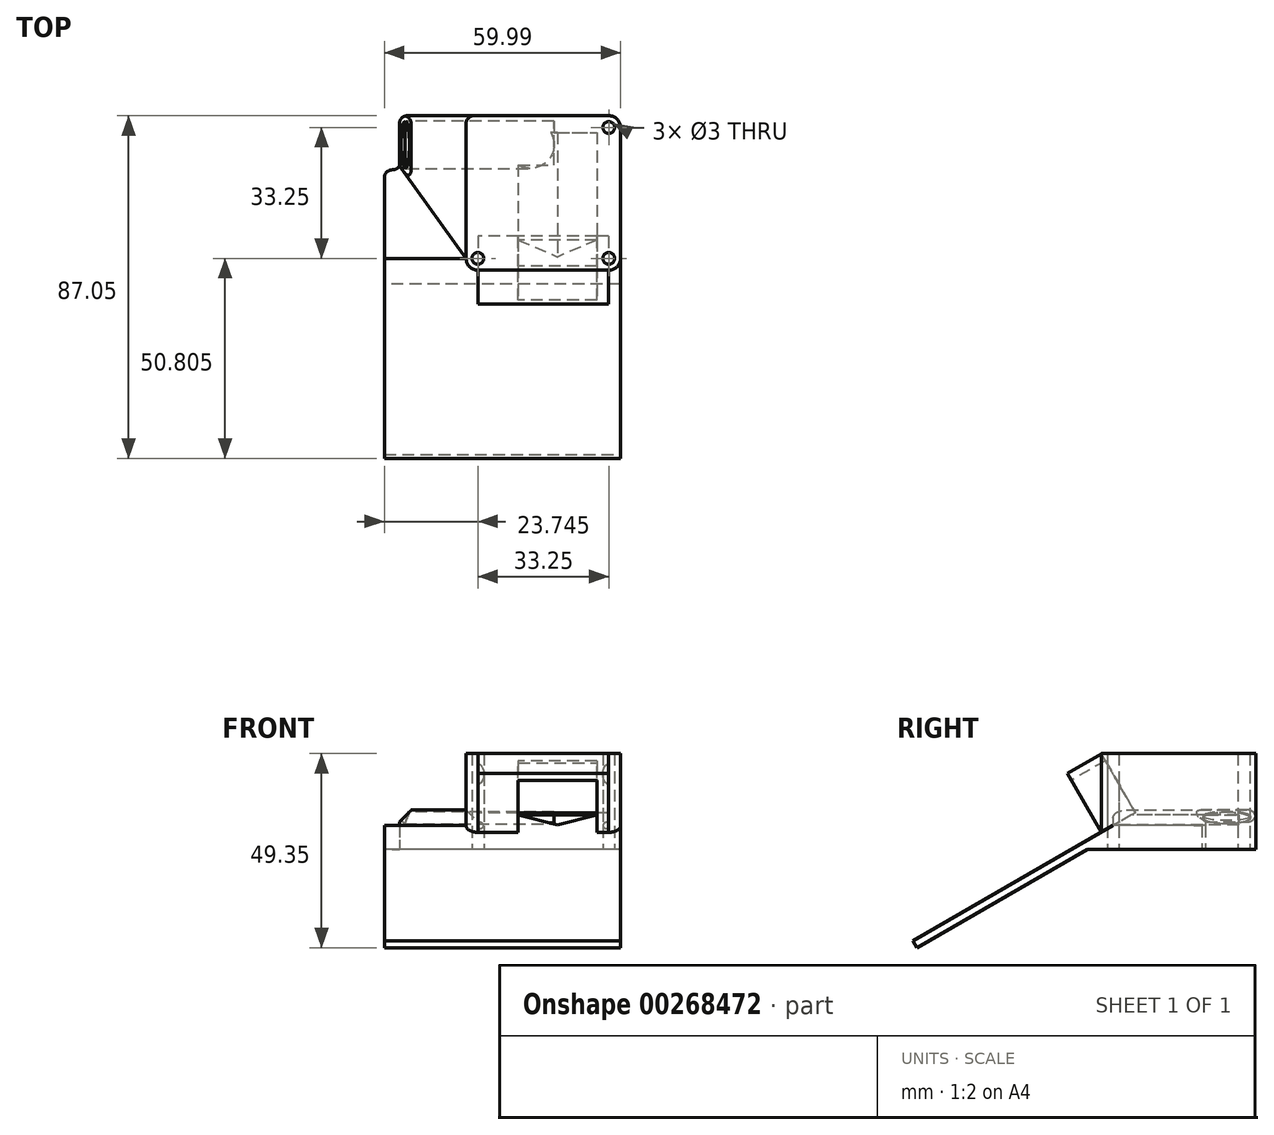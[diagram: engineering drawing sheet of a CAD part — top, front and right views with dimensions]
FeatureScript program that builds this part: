
annotation { "Feature Type Name" : "Feature", "Feature Type Description" : "" }
export const myFeature = defineFeature(function(context is Context, id is Id, definition is map)
    precondition{}
    {
        {
            var Q0;
            Q0=qCreatedBy(makeId("Top.planeOp"),FACE);
            var sketch = newSketch(context, id + "F0", { "sketchPlane" : qUnion([Q0])});
            skLineSegment(sketch, "E0.bottom", {"start": v(34.17, 23.12) * mm, "end": v(-34.17, 23.12) * mm});
            skLineSegment(sketch, "E0.top", {"start": v(34.17, -23.12) * mm, "end": v(-34.17, -23.12) * mm});
            skLineSegment(sketch, "E0.left", {"start": v(34.17, 23.12) * mm, "end": v(34.17, -23.12) * mm});
            skLineSegment(sketch, "E0.right", {"start": v(-34.17, 23.12) * mm, "end": v(-34.17, -23.12) * mm});
            skPoint(sketch, "E0.middle", {"position": v(0, 0) * mm});
            skCircle(sketch, "E1", {"center": v(31.18, -16.62) * mm, "radius": 1.28 * mm});
            skLineSegment(sketch, "E2", {"start": v(-54.01, 0) * mm, "end": v(41.89, 0) * mm, "construction": true});
            skPoint(sketch, "E2.endSnap0", {"position": v(34.17, 0) * mm});
            skCircle(sketch, "E3.MirrorC", {"center": v(31.17, 16.63) * mm, "radius": 1.28 * mm});
            skCircle(sketch, "E4", {"center": v(-2.08, -16.62) * mm, "radius": 1.25 * mm});
            skCircle(sketch, "E5", {"center": v(-28.3, 15.75) * mm, "radius": 3.88 * mm});
            skCircle(sketch, "E6", {"center": v(-31.17, -14.12) * mm, "radius": 1.5 * mm});
            skCircle(sketch, "E7.0.1.0", {"center": v(-31.17, 5.88) * mm, "radius": 1.5 * mm});
            skCircle(sketch, "E7.1.0.0", {"center": v(-13.17, -14.12) * mm, "radius": 1.5 * mm});
            skCircle(sketch, "E7.1.1.0", {"center": v(-13.17, 5.88) * mm, "radius": 1.5 * mm});
            skLineSegment(sketch, "E7.direction1", {"start": v(-31.17, -14.12) * mm, "end": v(-13.17, -14.12) * mm, "construction": true});
            skLineSegment(sketch, "E7.direction2", {"start": v(-31.17, -14.12) * mm, "end": v(-31.17, 5.88) * mm, "construction": true});
            skCircle(sketch, "E8", {"center": v(15.67, 0) * mm, "radius": 7.5 * mm});
            skSolve(sketch);
        }
        {
            var Q0;
            Q0 = qSketchRegion(id + "F0", true);
            extrude(context, id + "F1", {"entities" : qUnion([Q0]), "depth" : 8 * mm, "offsetDistance" : 25 * mm});
        }
        {
            var Q0;
            Q0=makeQuery(id+"F1.opExtrude","CAP_FACE",FACE,{"disambiguationData":[OSD([sQuery(id+"F0.wireOp",EDGE,"E0.bottom"),sQuery(id+"F0.wireOp",EDGE,"E0.top"),sQuery(id+"F0.wireOp",EDGE,"E0.left"),sQuery(id+"F0.wireOp",EDGE,"E0.right"),sQuery(id+"F0.wireOp",EDGE,"E1"),sQuery(id+"F0.wireOp",EDGE,"E3.MirrorC"),sQuery(id+"F0.wireOp",EDGE,"E4"),sQuery(id+"F0.wireOp",EDGE,"E5"),sQuery(id+"F0.wireOp",EDGE,"E6"),sQuery(id+"F0.wireOp",EDGE,"E7.0.1.0"),sQuery(id+"F0.wireOp",EDGE,"E7.1.0.0"),sQuery(id+"F0.wireOp",EDGE,"E7.1.1.0"),sQuery(id+"F0.wireOp",EDGE,"E8")])],"isStart":false});
            var sketch = newSketch(context, id + "F2", { "sketchPlane" : qUnion([Q0])});
            skCircle(sketch, "E9", {"center": v(-2.08, -16.62) * mm, "radius": 3 * mm});
            skCircle(sketch, "E10", {"center": v(31.18, -16.62) * mm, "radius": 3 * mm});
            skCircle(sketch, "E11", {"center": v(31.17, 16.63) * mm, "radius": 3 * mm});
            skCircle(sketch, "E12", {"center": v(-2.08, -16.62) * mm, "radius": 1.5 * mm});
            skCircle(sketch, "E13", {"center": v(31.18, -16.62) * mm, "radius": 1.5 * mm});
            skCircle(sketch, "E14", {"center": v(31.17, 16.63) * mm, "radius": 1.5 * mm});
            skLineSegment(sketch, "E15.bottom", {"start": v(-2.08, -19.62) * mm, "end": v(31.17, -19.62) * mm});
            skLineSegment(sketch, "E16.left", {"start": v(-5.08, -16.62) * mm, "end": v(-5.08, 19.63) * mm});
            skLineSegment(sketch, "E17", {"start": v(34.17, -16.62) * mm, "end": v(34.17, 16.63) * mm});
            skLineSegment(sketch, "E18", {"start": v(31.17, 19.63) * mm, "end": v(-5.08, 19.63) * mm});
            skLineSegment(sketch, "E19.bottom", {"start": v(28.17, 16.63) * mm, "end": v(0.92, 16.63) * mm});
            skLineSegment(sketch, "E19.top", {"start": v(28.17, -16.62) * mm, "end": v(0.92, -16.62) * mm});
            skLineSegment(sketch, "E19.left", {"start": v(28.17, 16.63) * mm, "end": v(28.17, -16.62) * mm});
            skLineSegment(sketch, "E19.right", {"start": v(0.92, 16.63) * mm, "end": v(0.92, -16.62) * mm});
            skLineSegment(sketch, "E20", {"start": v(-5.08, -16.62) * mm, "end": v(-22, 6.86) * mm});
            skLineSegment(sketch, "E21", {"start": v(-22, 6.86) * mm, "end": v(-22, 19.63) * mm});
            skLineSegment(sketch, "E22", {"start": v(-22, 19.63) * mm, "end": v(-5.08, 19.63) * mm});
            skSolve(sketch);
        }
        {
            var Q0;
            Q0=makeQuery(id+"F2.imprint","IMPRINT",FACE,{"disambiguationData":[TD([[makeQuery(id+"F2.imprint","IMPRINT",EDGE,{"derivedFrom":sQuery(id+"F2.wireOp",EDGE,"E14")}),-1.0]])]});
            var Q1;
            Q1=makeQuery(id+"F2.imprint","IMPRINT",FACE,{"disambiguationData":[TD([[makeQuery(id+"F2.imprint","IMPRINT",EDGE,{"derivedFrom":sQuery(id+"F2.wireOp",EDGE,"E13")}),-1.0]])]});
            var Q2;
            {var subQ0=sQuery(id+"F2.wireOp",EDGE,"E17");Q2=makeQuery(id+"F2.imprint","IMPRINT",FACE,{"disambiguationData":[TD([[makeQuery(id+"F2.imprint","IMPRINT",EDGE,{"derivedFrom":subQ0}),-1.0]])]});}
            var Q3;
            {var subQ0=sQuery(id+"F2.wireOp",EDGE,"E16.left");Q3=makeQuery(id+"F2.imprint","IMPRINT",FACE,{"disambiguationData":[TD([[makeQuery(id+"F2.imprint","IMPRINT",EDGE,{"derivedFrom":subQ0}),-1.0]])]});}
            var Q4;
            Q4=makeQuery(id+"F2.imprint","IMPRINT",FACE,{"disambiguationData":[TD([[makeQuery(id+"F2.imprint","IMPRINT",EDGE,{"derivedFrom":sQuery(id+"F2.wireOp",EDGE,"E19.bottom")}),1.0]])]});
            var Q5;
            Q5=makeQuery(id+"F2.imprint","IMPRINT",FACE,{"disambiguationData":[TD([[makeQuery(id+"F2.imprint","IMPRINT",EDGE,{"derivedFrom":makeQuery(id+"F1.opExtrude","CAP_EDGE",EDGE,{"disambiguationData":[OSD([sQuery(id+"F0.wireOp",EDGE,"E8")])],"isStart":false})}),1.0]])]});
            var Q6;
            {var subQ0=sQuery(id+"F2.wireOp",EDGE,"E15.bottom");Q6=makeQuery(id+"F2.imprint","IMPRINT",FACE,{"disambiguationData":[TD([[makeQuery(id+"F2.imprint","IMPRINT",EDGE,{"derivedFrom":subQ0}),1.0]])]});}
            var Q7;
            Q7=makeQuery(id+"F2.imprint","IMPRINT",FACE,{"disambiguationData":[TD([[makeQuery(id+"F2.imprint","IMPRINT",EDGE,{"derivedFrom":sQuery(id+"F2.wireOp",EDGE,"E12")}),-1.0]])]});
            extrude(context, id + "F3", {"entities" : qUnion([Q0, Q1, Q2, Q3, Q4, Q5, Q6, Q7]), "operationType" : NewBodyOperationType.ADD, "depth" : 24.35 * mm, "offsetDistance" : 25 * mm});
        }
        {
            var Q0;
            Q0=makeQuery(id+"F3.boolean.opBoolean","MERGE",FACE,{"derivedFrom":[makeQuery(id+"F1.opExtrude","SWEPT_FACE",FACE,{"disambiguationData":[OSD([sQuery(id+"F0.wireOp",EDGE,"E0.left")])]}),makeQuery(id+"F3.opExtrude","SWEPT_FACE",FACE,{"disambiguationData":[OSD([sQuery(id+"F2.wireOp",EDGE,"E17")])]})]});
            var sketch = newSketch(context, id + "F4", { "sketchPlane" : qUnion([Q0])});
            skLineSegment(sketch, "E23", {"start": v(-23.12, 8) * mm, "end": v(-66.43, -17) * mm});
            skLineSegment(sketch, "E24", {"start": v(-23.12, 8) * mm, "end": v(-16.62, 11.75) * mm});
            skLineSegment(sketch, "E25", {"start": v(-66.43, -17) * mm, "end": v(-67.43, -15.27) * mm});
            skLineSegment(sketch, "E26", {"start": v(-67.43, -15.27) * mm, "end": v(-16.62, 14.06) * mm});
            skLineSegment(sketch, "E27", {"start": v(-16.62, 14.06) * mm, "end": v(-16.62, 11.75) * mm});
            skLineSegment(sketch, "E28", {"start": v(-16.62, 11.75) * mm, "end": v(-16.62, 8) * mm});
            skLineSegment(sketch, "E29", {"start": v(-16.62, 8) * mm, "end": v(-23.12, 8) * mm});
            skSolve(sketch);
        }
        {
            var Q0;
            Q0 = qSketchRegion(id + "F4", true);
            extrude(context, id + "F5", {"entities" : qUnion([Q0]), "operationType" : NewBodyOperationType.ADD, "oppositeDirection" : true, "depth" : 60 * mm, "offsetDistance" : 25 * mm});
        }
        {
            var Q0;
            {var subQ3=sQuery(id+"F4.wireOp",EDGE,"E26");Q0=makeQuery(id+"F5.boolean.opBoolean","SPLIT",FACE,{"disambiguationData":[TD([makeQuery(id+"F1.opExtrude","SWEPT_FACE",FACE,{"disambiguationData":[OSD([sQuery(id+"F0.wireOp",EDGE,"E0.left")])]})])],"derivedFrom":makeQuery(id+"F5.opExtrude","SWEPT_FACE",FACE,{"disambiguationData":[OSD([subQ3])]})});}
            var sketch = newSketch(context, id + "F6", { "sketchPlane" : qUnion([Q0])});
            skLineSegment(sketch, "E30.bottom", {"start": v(28.17, -10.83) * mm, "end": v(8.17, -10.83) * mm});
            skLineSegment(sketch, "E30.top", {"start": v(28.17, -16.91) * mm, "end": v(8.18, -16.91) * mm});
            skLineSegment(sketch, "E30.left", {"start": v(28.17, -10.83) * mm, "end": v(28.17, -16.91) * mm});
            skLineSegment(sketch, "E30.right", {"start": v(8.17, -10.83) * mm, "end": v(8.18, -16.91) * mm});
            skSolve(sketch);
        }
        {
            var Q0;
            Q0=makeQuery(id+"F6.imprint","IMPRINT",FACE,{"disambiguationData":[TD([[makeQuery(id+"F6.imprint","IMPRINT",EDGE,{"derivedFrom":sQuery(id+"F6.wireOp",EDGE,"E30.bottom")}),1.0]])]});
            extrude(context, id + "F7", {"entities" : qUnion([Q0]), "operationType" : NewBodyOperationType.ADD, "depth" : 15.25 * mm, "offsetDistance" : 25 * mm});
        }
        {
            var Q0;
            Q0=makeQuery(id+"F7.opExtrude","SWEPT_FACE",FACE,{"disambiguationData":[OSD([sQuery(id+"F6.wireOp",EDGE,"E30.bottom")])]});
            var sketch = newSketch(context, id + "F8", { "sketchPlane" : qUnion([Q0])});
            skLineSegment(sketch, "E31.bottom", {"start": v(-28.17, 20.5) * mm, "end": v(-8.17, 20.5) * mm});
            skLineSegment(sketch, "E31.top", {"start": v(-28.18, 35.74) * mm, "end": v(-8.17, 35.74) * mm});
            skLineSegment(sketch, "E31.left", {"start": v(-28.18, 20.5) * mm, "end": v(-28.18, 35.74) * mm});
            skLineSegment(sketch, "E31.right", {"start": v(-8.17, 20.5) * mm, "end": v(-8.17, 35.74) * mm});
            skLineSegment(sketch, "E32.bottom", {"start": v(-31.17, 20.5) * mm, "end": v(2.05, 20.5) * mm});
            skLineSegment(sketch, "E32.top", {"start": v(-31.17, 35.74) * mm, "end": v(2.05, 35.74) * mm});
            skLineSegment(sketch, "E32.left", {"start": v(-31.17, 20.5) * mm, "end": v(-31.17, 35.74) * mm});
            skLineSegment(sketch, "E32.right", {"start": v(2.05, 20.5) * mm, "end": v(2.05, 35.74) * mm});
            skLineSegment(sketch, "E33.bottom", {"start": v(2.05, 35.74) * mm, "end": v(-31.17, 35.74) * mm});
            skLineSegment(sketch, "E33.top", {"start": v(2.05, 37.74) * mm, "end": v(-31.17, 37.74) * mm});
            skLineSegment(sketch, "E33.left", {"start": v(2.05, 35.74) * mm, "end": v(2.05, 37.74) * mm});
            skLineSegment(sketch, "E33.right", {"start": v(-31.17, 35.74) * mm, "end": v(-31.17, 37.74) * mm});
            skSolve(sketch);
        }
        {
            var Q0;
            Q0 = qSketchRegion(id + "F6", true);
            extrude(context, id + "F9", {"entities" : qUnion([Q0]), "operationType" : NewBodyOperationType.REMOVE, "depth" : 25 * mm, "offsetDistance" : 25 * mm});
        }
        {
            var Q0;
            {var subQ0=sQuery(id+"F8.wireOp",EDGE,"E31.right");Q0=makeQuery(id+"F8.imprint","IMPRINT",FACE,{"disambiguationData":[TD([[makeQuery(id+"F8.imprint","IMPRINT",EDGE,{"derivedFrom":subQ0}),1.0]])]});}
            var Q1;
            {var subQ0=sQuery(id+"F8.wireOp",EDGE,"E31.left");Q1=makeQuery(id+"F8.imprint","IMPRINT",FACE,{"disambiguationData":[TD([[makeQuery(id+"F8.imprint","IMPRINT",EDGE,{"derivedFrom":subQ0}),-1.0]])]});}
            var Q2;
            Q2=makeQuery(id+"F8.imprint","IMPRINT",FACE,{"disambiguationData":[TD([[makeQuery(id+"F8.imprint","IMPRINT",EDGE,{"derivedFrom":sQuery(id+"F8.wireOp",EDGE,"E33.top")}),1.0]])]});
            extrude(context, id + "F10", {"entities" : qUnion([Q0, Q1, Q2]), "depth" : 10 * mm, "offsetDistance" : 25 * mm});
        }
        {
            var Q0;
            {var subQ0=sQuery(id+"F8.wireOp",EDGE,"E31.left");Q0=makeQuery(id+"F8.imprint","IMPRINT",FACE,{"disambiguationData":[TD([[makeQuery(id+"F8.imprint","IMPRINT",EDGE,{"derivedFrom":subQ0}),1.0]])]});}
            extrude(context, id + "F11", {"entities" : qUnion([Q0]), "operationType" : NewBodyOperationType.REMOVE, "depth" : 10 * mm, "offsetDistance" : 25 * mm});
        }
        {
            var Q0;
            Q0=makeQuery(id+"F2.imprint","IMPRINT",FACE,{"disambiguationData":[TD([[makeQuery(id+"F2.imprint","IMPRINT",EDGE,{"derivedFrom":sQuery(id+"F2.wireOp",EDGE,"E16.left")}),1.0]])]});
            var Q1;
            Q1=makeQuery(id+"F2.imprint","IMPRINT",FACE,{"disambiguationData":[TD([[makeQuery(id+"F2.imprint","IMPRINT",EDGE,{"derivedFrom":makeQuery(id+"F1.opExtrude","CAP_EDGE",EDGE,{"disambiguationData":[OSD([sQuery(id+"F0.wireOp",EDGE,"E7.1.1.0")])],"isStart":false})}),1.0]])]});
            extrude(context, id + "F12", {"entities" : qUnion([Q0, Q1]), "operationType" : NewBodyOperationType.ADD, "depth" : 10 * mm, "offsetDistance" : 25 * mm});
        }
        {
            var Q0;
            Q0=makeQuery(id+"F12.opExtrude","CAP_EDGE",EDGE,{"disambiguationData":[OSD([sQuery(id+"F2.wireOp",EDGE,"E21")])],"isStart":false});
            chamfer(context, id + "F13", {"entities" : qUnion([Q0]), "width" : 3 * mm, "tangentPropagation" : true});
        }
        {
            var Q0;
            Q0=makeQuery(id+"F12.opExtrude","CAP_EDGE",EDGE,{"disambiguationData":[OSD([sQuery(id+"F2.wireOp",EDGE,"E22")])],"isStart":false});
            var Q1;
            Q1=makeQuery(id+"F3.opExtrude","SWEPT_EDGE",EDGE,{"disambiguationData":[OSD([sQuery(id+"F2.wireOp",EDGE,"E16.left"),sQuery(id+"F2.wireOp",EDGE,"E18"),sQuery(id+"F2.wireOp",EDGE,"E22")])]});
            var Q2;
            Q2=makeQuery(id+"F12.opExtrude","CAP_EDGE",EDGE,{"disambiguationData":[OSD([sQuery(id+"F2.wireOp",EDGE,"E20")])],"isStart":false});
            var Q3;
            Q3=makeQuery(id+"F12.opExtrude","SWEPT_EDGE",EDGE,{"disambiguationData":[OSD([sQuery(id+"F2.wireOp",EDGE,"E21"),sQuery(id+"F2.wireOp",EDGE,"E22")])]});
            fillet(context, id + "F14", {"entities" : qUnion([Q0, Q1, Q2, Q3]), "radius" : 2 * mm, "tangentPropagation" : true, "allowEdgeOverflow" : false});
        }
        {
            var Q0;
            Q0=makeQuery(id+"F13.opChamfer","BLEND_FACE",FACE,{"disambiguationData":[OSD([sQuery(id+"F2.wireOp",EDGE,"E21")])]});
            var sketch = newSketch(context, id + "F15", { "sketchPlane" : qUnion([Q0])});
            skEllipse(sketch, "E34", {"center": v(-12.24, -2.83) * mm, "majorRadius": 6 * mm, "minorRadius": 1.5 * mm, "majorAxis": v(-1, 0)});
            skPoint(sketch, "E34.centerSnap0", {"position": v(-12.24, -4.96) * mm});
            skSolve(sketch);
        }
        {
            var Q0;
            Q0=makeQuery(id+"F3.opExtrude","SWEPT_FACE",FACE,{"disambiguationData":[OSD([sQuery(id+"F2.wireOp",EDGE,"E15.bottom")])]});
            var sketch = newSketch(context, id + "F16", { "sketchPlane" : qUnion([Q0])});
            skPoint(sketch, "E35", {"position": v(28.17, 16.78) * mm});
            skPoint(sketch, "E36", {"position": v(8.17, 16.78) * mm});
            skLineSegment(sketch, "E37.bottom", {"start": v(28.17, 16.78) * mm, "end": v(8.17, 16.78) * mm, "construction": true});
            skLineSegment(sketch, "E37.top", {"start": v(28.17, 14.28) * mm, "end": v(8.17, 14.28) * mm, "construction": true});
            skLineSegment(sketch, "E37.left", {"start": v(28.17, 16.78) * mm, "end": v(28.17, 14.28) * mm, "construction": true});
            skLineSegment(sketch, "E37.right", {"start": v(8.17, 16.78) * mm, "end": v(8.17, 14.28) * mm, "construction": true});
            skLineSegment(sketch, "E38", {"start": v(8.17, 16.78) * mm, "end": v(28.18, 16.78) * mm});
            skLineSegment(sketch, "E39", {"start": v(18.17, 14.28) * mm, "end": v(8.17, 16.78) * mm});
            skLineSegment(sketch, "E40", {"start": v(18.17, 14.28) * mm, "end": v(28.17, 16.78) * mm});
            skSolve(sketch);
        }
        {
            var Q0;
            Q0 = qSketchRegion(id + "F16", true);
            extrude(context, id + "F17", {"entities" : qUnion([Q0]), "operationType" : NewBodyOperationType.REMOVE, "oppositeDirection" : true, "depth" : 35 * mm, "offsetDistance" : 25 * mm});
        }
        {
            var Q0;
            Q0=makeQuery(id+"F12.boolean.opBoolean","MERGE",FACE,{"derivedFrom":[makeQuery(id+"F3.opExtrude","SWEPT_FACE",FACE,{"disambiguationData":[OSD([sQuery(id+"F2.wireOp",EDGE,"E18")])]}),makeQuery(id+"F12.opExtrude","SWEPT_FACE",FACE,{"disambiguationData":[OSD([sQuery(id+"F2.wireOp",EDGE,"E22")])]})]});
            var sketch = newSketch(context, id + "F18", { "sketchPlane" : qUnion([Q0])});
            skLineSegment(sketch, "E41", {"start": v(21.71, 17.7) * mm, "end": v(20, 16) * mm});
            skLineSegment(sketch, "E42", {"start": v(20, 16) * mm, "end": v(-17.24, 16) * mm});
            skSolve(sketch);
        }
        {
            var Q0;
            Q0=makeQuery(id+"F15.imprint","IMPRINT",FACE,{"disambiguationData":[TD([[makeQuery(id+"F15.imprint","IMPRINT",EDGE,{"derivedFrom":sQuery(id+"F15.wireOp",EDGE,"E34")}),1.0]])]});
            var Q1;
            Q1=sQuery(id+"F18.wireOp",EDGE,"CqFdQHIr-c7NS-FuwX-CuOY-meUfU1ydqvjM");
            var Q2;
            Q2=sQuery(id+"F18.wireOp",EDGE,"E42");
            var Q3;
            Q3=sQuery(id+"F18.wireOp",EDGE,"E41");
            sweep(context, id + "F19", {"operationType" : NewBodyOperationType.REMOVE, "profiles" : qUnion([Q0]), "path" : qUnion([Q1, Q2, Q3])});
        }
        {
            var Q0;
            Q0=makeQuery(id+"F2.imprint","IMPRINT",FACE,{"disambiguationData":[TD([[makeQuery(id+"F2.imprint","IMPRINT",EDGE,{"derivedFrom":makeQuery(id+"F1.opExtrude","CAP_EDGE",EDGE,{"disambiguationData":[OSD([sQuery(id+"F0.wireOp",EDGE,"E4")])],"isStart":false})}),1.0]])]});
            var Q1;
            Q1=makeQuery(id+"F2.imprint","IMPRINT",FACE,{"disambiguationData":[TD([[makeQuery(id+"F2.imprint","IMPRINT",EDGE,{"derivedFrom":sQuery(id+"F2.wireOp",EDGE,"E12")}),1.0]])]});
            var Q2;
            Q2=makeQuery(id+"F2.imprint","IMPRINT",FACE,{"disambiguationData":[TD([[makeQuery(id+"F2.imprint","IMPRINT",EDGE,{"derivedFrom":sQuery(id+"F2.wireOp",EDGE,"E13")}),1.0]])]});
            var Q3;
            Q3=makeQuery(id+"F2.imprint","IMPRINT",FACE,{"disambiguationData":[TD([[makeQuery(id+"F2.imprint","IMPRINT",EDGE,{"derivedFrom":makeQuery(id+"F1.opExtrude","CAP_EDGE",EDGE,{"disambiguationData":[OSD([sQuery(id+"F0.wireOp",EDGE,"E1")])],"isStart":false})}),1.0]])]});
            extrude(context, id + "F20", {"entities" : qUnion([Q0, Q1, Q2, Q3]), "operationType" : NewBodyOperationType.REMOVE, "depth" : 25 * mm, "offsetDistance" : 25 * mm});
        }
        {
            var Q0;
            Q0 = qSketchRegion(id + "F0", true);
            extrude(context, id + "F21", {"entities" : qUnion([Q0]), "operationType" : NewBodyOperationType.REMOVE, "depth" : 8 * mm, "offsetDistance" : 25 * mm});
        }
        {
            var Q0;
            {var subQ0=sQuery(id+"F4.wireOp",EDGE,"E28");var subQ1=sQuery(id+"F4.wireOp",EDGE,"E27");Q0=makeQuery(id+"F5.boolean.opBoolean","SPLIT",FACE,{"disambiguationData":[TD([makeQuery(id+"F3.opExtrude","SWEPT_FACE",FACE,{"disambiguationData":[OSD([sQuery(id+"F2.wireOp",EDGE,"E9")])]})])],"derivedFrom":makeQuery(id+"F5.opExtrude","SWEPT_FACE",FACE,{"disambiguationData":[OSD([subQ1,subQ0])]})});}
            var sketch = newSketch(context, id + "F22", { "sketchPlane" : qUnion([Q0])});
            skLineSegment(sketch, "E43.bottom", {"start": v(25.82, 14.06) * mm, "end": v(5.08, 14.06) * mm});
            skLineSegment(sketch, "E43.top", {"start": v(25.82, 8) * mm, "end": v(5.08, 8) * mm});
            skLineSegment(sketch, "E43.left", {"start": v(25.82, 14.06) * mm, "end": v(25.82, 8) * mm});
            skLineSegment(sketch, "E43.right", {"start": v(5.08, 14.06) * mm, "end": v(5.08, 8) * mm});
            skSolve(sketch);
        }
        {
            var Q0;
            Q0 = qSketchRegion(id + "F22", true);
            extrude(context, id + "F23", {"entities" : qUnion([Q0]), "operationType" : NewBodyOperationType.ADD, "depth" : 22.5 * mm, "offsetDistance" : 25 * mm});
        }
        {
            var Q0;
            Q0=makeQuery(id+"F23.boolean.opBoolean","INTERSECT",EDGE,{"derivedFrom":[makeQuery(id+"F12.opExtrude","SWEPT_FACE",FACE,{"disambiguationData":[OSD([sQuery(id+"F2.wireOp",EDGE,"E20")])]}),makeQuery(id+"F23.opExtrude","CAP_FACE",FACE,{"disambiguationData":[OSD([sQuery(id+"F22.wireOp",EDGE,"E43.bottom"),sQuery(id+"F22.wireOp",EDGE,"E43.top"),sQuery(id+"F22.wireOp",EDGE,"E43.left"),sQuery(id+"F22.wireOp",EDGE,"E43.right")])],"isStart":false})]});
            var Q1;
            Q1=makeQuery(id+"F23.opExtrude","CAP_EDGE",EDGE,{"disambiguationData":[OSD([sQuery(id+"F22.wireOp",EDGE,"E43.left")])],"isStart":false});
            fillet(context, id + "F24", {"entities" : qUnion([Q0, Q1]), "radius" : 2 * mm, "tangentPropagation" : true, "allowEdgeOverflow" : false});
        }
    });
